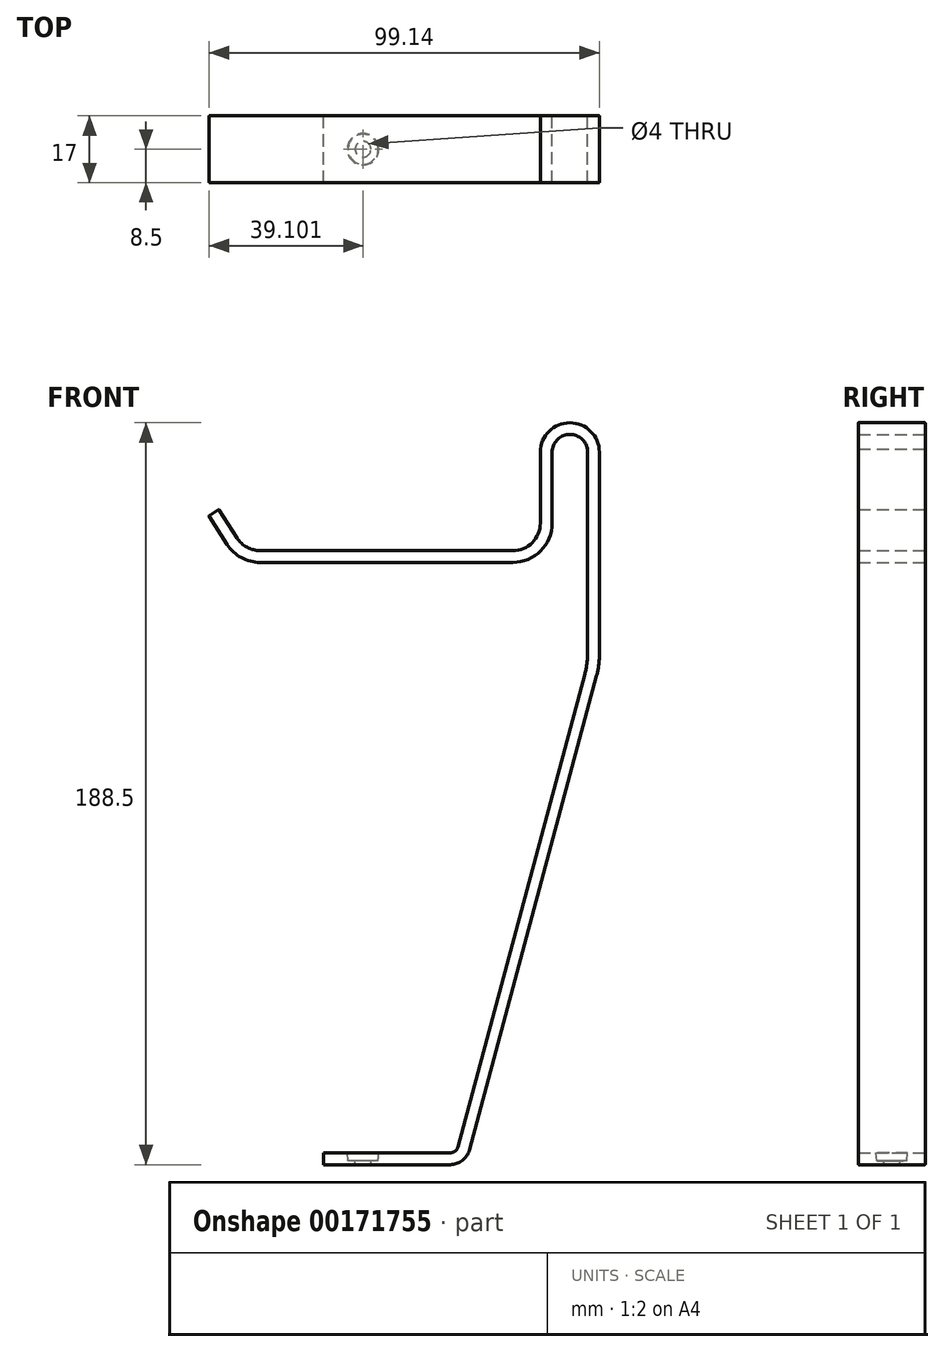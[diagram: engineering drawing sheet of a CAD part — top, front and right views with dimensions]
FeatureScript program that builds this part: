
annotation { "Feature Type Name" : "Feature", "Feature Type Description" : "" }
export const myFeature = defineFeature(function(context is Context, id is Id, definition is map)
    precondition{}
    {
        {
            var Q0;
            Q0=qCreatedBy(makeId("Front.planeOp"),FACE);
            var sketch = newSketch(context, id + "F0", { "sketchPlane" : qUnion([Q0])});
            skLineSegment(sketch, "E0", {"start": v(-77.45, -70.7) * mm, "end": v(-45.28, -70.7) * mm});
            skLineSegment(sketch, "E1", {"start": v(-40.46, -67) * mm, "end": v(-8.1, 53.55) * mm});
            skLineSegment(sketch, "E2", {"start": v(-7.41, 58.74) * mm, "end": v(-7.41, 110.3) * mm});
            skLineSegment(sketch, "E3", {"start": v(-7.41, 110.3) * mm, "end": v(-10.41, 110.3) * mm});
            skLineSegment(sketch, "E4", {"start": v(-22.41, 110.3) * mm, "end": v(-22.41, 92.3) * mm});
            skLineSegment(sketch, "E5", {"start": v(-29.41, 85.3) * mm, "end": v(-93.57, 85.3) * mm});
            skPoint(sketch, "E6.visualSharp", {"position": v(-41.45, -70.7) * mm});
            skArc(sketch, "E6.filletArc", {"start": v(-45.28, -70.7) * mm, "mid": v(-42.24, -69.68) * mm, "end": v(-40.46, -67) * mm});
            skArc(sketch, "E7", {"start": v(-7.41, 110.3) * mm, "mid": v(-14.91, 117.8) * mm, "end": v(-22.41, 110.3) * mm});
            skPoint(sketch, "E8.visualSharp", {"position": v(-7.41, 56.1) * mm});
            skArc(sketch, "E8.filletArc", {"start": v(-8.1, 53.55) * mm, "mid": v(-7.59, 56.12) * mm, "end": v(-7.41, 58.74) * mm});
            skPoint(sketch, "E9.visualSharp", {"position": v(-22.41, 85.3) * mm});
            skArc(sketch, "E9.filletArc", {"start": v(-29.41, 85.3) * mm, "mid": v(-24.46, 87.34) * mm, "end": v(-22.41, 92.3) * mm});
            skLineSegment(sketch, "E10", {"start": v(-99.48, 88.53) * mm, "end": v(-104.06, 95.74) * mm});
            skPoint(sketch, "E11.visualSharp", {"position": v(-97.41, 85.3) * mm});
            skArc(sketch, "E11.filletArc", {"start": v(-99.48, 88.53) * mm, "mid": v(-96.94, 86.15) * mm, "end": v(-93.57, 85.3) * mm});
            skLineSegment(sketch, "E12", {"start": v(-77.45, -70.7) * mm, "end": v(-77.45, -67.7) * mm});
            skLineSegment(sketch, "E13", {"start": v(-77.45, -67.7) * mm, "end": v(-45.28, -67.7) * mm});
            skLineSegment(sketch, "E14", {"start": v(-43.35, -66.23) * mm, "end": v(-11.1, 53.95) * mm});
            skLineSegment(sketch, "E15", {"start": v(-10.41, 59.13) * mm, "end": v(-10.41, 111.1) * mm});
            skLineSegment(sketch, "E16", {"start": v(-19.41, 92.3) * mm, "end": v(-19.41, 110.3) * mm});
            skArc(sketch, "E17", {"start": v(-10.41, 111.1) * mm, "mid": v(-15.28, 114.8) * mm, "end": v(-19.41, 110.3) * mm});
            skLineSegment(sketch, "E18", {"start": v(-93.57, 82.3) * mm, "end": v(-29.41, 82.3) * mm});
            skArc(sketch, "E19", {"start": v(-29.41, 82.3) * mm, "mid": v(-22.34, 85.22) * mm, "end": v(-19.41, 92.3) * mm});
            skLineSegment(sketch, "E20", {"start": v(-104.06, 95.74) * mm, "end": v(-106.6, 94.13) * mm});
            skLineSegment(sketch, "E21", {"start": v(-106.6, 94.13) * mm, "end": v(-101.98, 86.88) * mm});
            skArc(sketch, "E22", {"start": v(-101.98, 86.88) * mm, "mid": v(-98.36, 83.51) * mm, "end": v(-93.57, 82.3) * mm});
            skPoint(sketch, "E23.visualSharp", {"position": v(-10.41, 56.5) * mm});
            skArc(sketch, "E23.filletArc", {"start": v(-11.1, 53.95) * mm, "mid": v(-10.59, 56.52) * mm, "end": v(-10.41, 59.13) * mm});
            skPoint(sketch, "E24.visualSharp", {"position": v(-43.75, -67.7) * mm});
            skArc(sketch, "E24.filletArc", {"start": v(-45.28, -67.7) * mm, "mid": v(-44.07, -67.3) * mm, "end": v(-43.35, -66.23) * mm});
            skLineSegment(sketch, "E25.trimOffspring", {"start": v(-19.41, 110.3) * mm, "end": v(-22.41, 110.3) * mm});
            skSolve(sketch);
        }
        {
            var Q0;
            Q0=makeQuery(id+"F0.imprint","IMPRINT",FACE,{"disambiguationData":[TD([[makeQuery(id+"F0.imprint","IMPRINT",EDGE,{"derivedFrom":sQuery(id+"F0.wireOp",EDGE,"E0")}),1.0]])]});
            var Q1;
            {var subQ2=sQuery(id+"F0.wireOp",EDGE,"E3");Q1=makeQuery(id+"F0.imprint","IMPRINT",FACE,{"disambiguationData":[TD([[makeQuery(id+"F0.imprint","IMPRINT",EDGE,{"derivedFrom":subQ2}),-1.0]])]});}
            var Q2;
            Q2=makeQuery(id+"F0.imprint","IMPRINT",FACE,{"disambiguationData":[TD([[makeQuery(id+"F0.imprint","IMPRINT",EDGE,{"derivedFrom":sQuery(id+"F0.wireOp",EDGE,"E4")}),1.0]])]});
            extrude(context, id + "F1", {"entities" : qUnion([Q0, Q1, Q2]), "depth" : 17 * mm});
        }
        {
            var Q0;
            Q0=makeQuery(id+"F1.opExtrude","SWEPT_FACE",FACE,{"disambiguationData":[OSD([sQuery(id+"F0.wireOp",EDGE,"E13")])]});
            var sketch = newSketch(context, id + "F2", { "sketchPlane" : qUnion([Q0])});
            skLineSegment(sketch, "E26", {"start": v(-77.45, -8.5) * mm, "end": v(-67.45, -8.5) * mm, "construction": true});
            skCircle(sketch, "E27", {"center": v(-67.45, -8.5) * mm, "radius": 2 * mm});
            skSolve(sketch);
        }
        {
            var Q0;
            Q0 = qSketchRegion(id + "F2", true);
            extrude(context, id + "F3", {"entities" : qUnion([Q0]), "operationType" : NewBodyOperationType.REMOVE, "endBound" : BoundingType.THROUGH_ALL, "oppositeDirection" : true, "depth" : 25 * mm});
        }
        {
            var Q0;
            Q0=makeQuery(id+"F1.opExtrude","SWEPT_FACE",FACE,{"disambiguationData":[OSD([sQuery(id+"F0.wireOp",EDGE,"E13")])]});
            var sketch = newSketch(context, id + "F4", { "sketchPlane" : qUnion([Q0])});
            skCircle(sketch, "E28", {"center": v(-67.45, -8.5) * mm, "radius": 4 * mm});
            skSolve(sketch);
        }
        {
            var Q0;
            Q0 = qSketchRegion(id + "F4", true);
            extrude(context, id + "F5", {"entities" : qUnion([Q0]), "operationType" : NewBodyOperationType.REMOVE, "oppositeDirection" : true, "depth" : 2 * mm, "hasDraft" : true, "draftAngle" : 5 * degree, "draftPullDirection" : true});
        }
        {
            var Q0;
            Q0=makeQuery(id+"F1.opExtrude","SWEPT_EDGE",EDGE,{"disambiguationData":[OSD([sQuery(id+"F0.wireOp",EDGE,"E10"),sQuery(id+"F0.wireOp",EDGE,"E20")])]});
            var Q1;
            Q1=makeQuery(id+"F1.opExtrude","SWEPT_EDGE",EDGE,{"disambiguationData":[OSD([sQuery(id+"F0.wireOp",EDGE,"E20"),sQuery(id+"F0.wireOp",EDGE,"E21")])]});
            var Q2;
            Q2=makeQuery(id+"F1.opExtrude","CAP_EDGE",EDGE,{"disambiguationData":[OSD([sQuery(id+"F0.wireOp",EDGE,"E21")])],"isStart":false});
            var Q3;
            Q3=makeQuery(id+"F1.opExtrude","CAP_EDGE",EDGE,{"disambiguationData":[OSD([sQuery(id+"F0.wireOp",EDGE,"E10")])],"isStart":false});
            var Q4;
            Q4=makeQuery(id+"F1.opExtrude","CAP_EDGE",EDGE,{"disambiguationData":[OSD([sQuery(id+"F0.wireOp",EDGE,"E10")])],"isStart":true});
            var Q5;
            Q5=makeQuery(id+"F1.opExtrude","CAP_EDGE",EDGE,{"disambiguationData":[OSD([sQuery(id+"F0.wireOp",EDGE,"E20")])],"isStart":true});
            var Q6;
            Q6=makeQuery(id+"F1.opExtrude","CAP_EDGE",EDGE,{"disambiguationData":[OSD([sQuery(id+"F0.wireOp",EDGE,"E20")])],"isStart":false});
            var Q7;
            Q7=makeQuery(id+"F1.opExtrude","CAP_EDGE",EDGE,{"disambiguationData":[OSD([sQuery(id+"F0.wireOp",EDGE,"E22")])],"isStart":false});
            var Q8;
            Q8=makeQuery(id+"F1.opExtrude","CAP_EDGE",EDGE,{"disambiguationData":[OSD([sQuery(id+"F0.wireOp",EDGE,"E18")])],"isStart":false});
            var Q9;
            Q9=makeQuery(id+"F1.opExtrude","CAP_EDGE",EDGE,{"disambiguationData":[OSD([sQuery(id+"F0.wireOp",EDGE,"E18")])],"isStart":true});
            fillet(context, id + "F6", {"entities" : qUnion([Q0, Q1, Q2, Q3, Q4, Q5, Q6, Q7, Q8, Q9]), "radius" : 0.1 * mm, "tangentPropagation" : true, "allowEdgeOverflow" : false});
        }
    });
